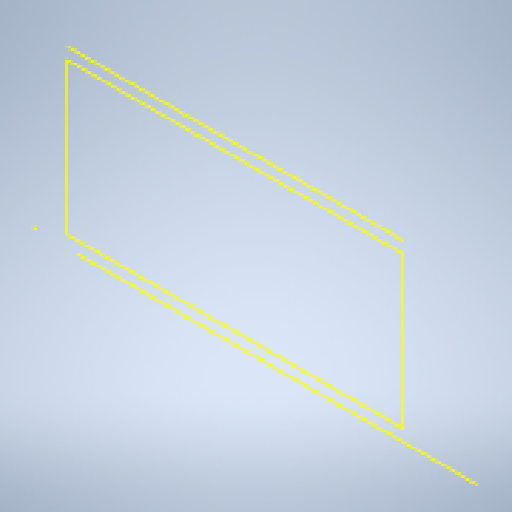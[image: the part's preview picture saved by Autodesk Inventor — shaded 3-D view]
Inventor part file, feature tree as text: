
AUTODESK INVENTOR PART (.ipt)
format: ipt  version: 2023 (Build 270158030, 158C)  size: 125,952 bytes
history: native  units: mm
features: reference x3, other x3, sketch x1
ambient origin geometry x8: Origin, YZ Plane, XZ Plane, XY Plane, X Axis, Y Axis, Z Axis, Center Point
feature tree (7):
  sketch  "Sketch1"
  reference  "Reference1"
  reference  "Reference2"
  reference  "Reference3"
  other  "<userpath>\Documents\0004-inventor\3D-CAD-main\cable-hanger\cable-hanger-hook.iam"
  other  "cable-hanger-hook.iam"
  other  "cable-hanger:1"
